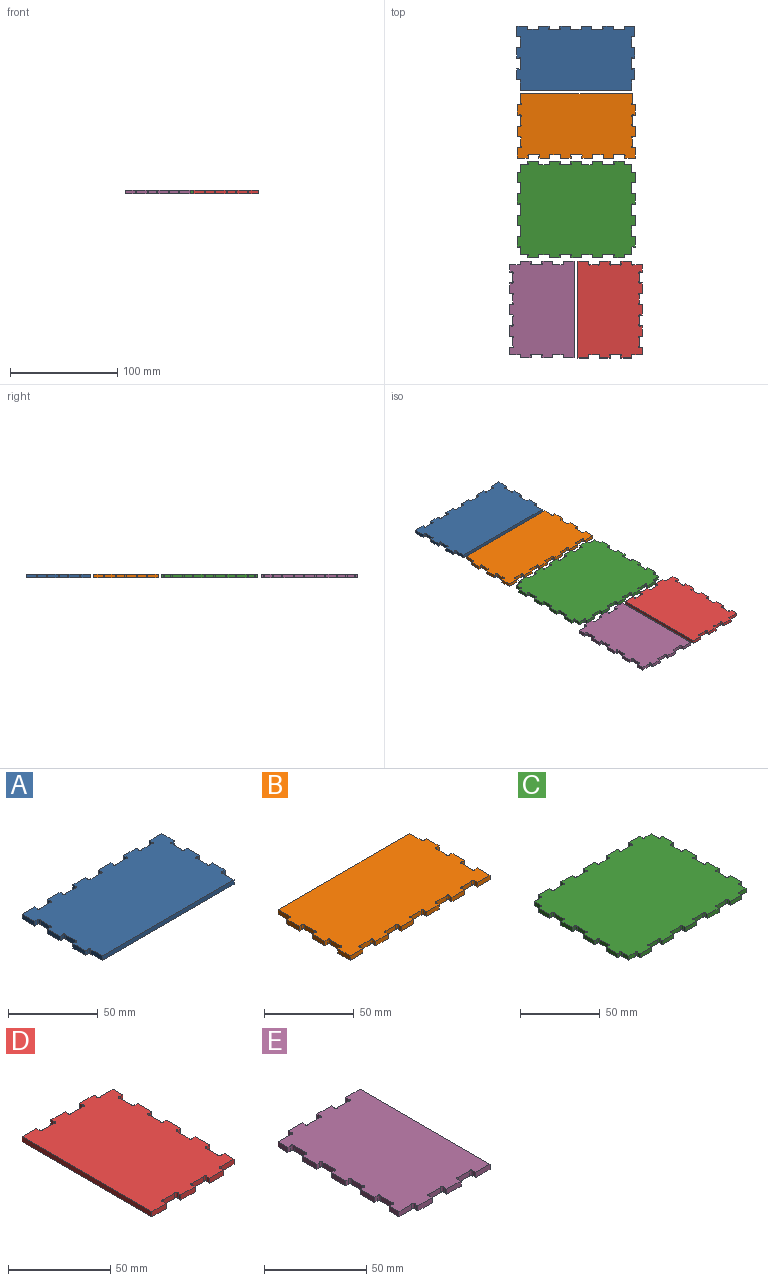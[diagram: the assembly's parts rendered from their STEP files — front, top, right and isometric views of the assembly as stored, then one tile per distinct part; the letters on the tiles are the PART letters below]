
ASSEMBLY  parts=5 mates=4
PART A: 66 faces, bbox 110x60x3.1 mm
  f0: plane 110x60mm, normal (0,0,-1), area 6247.3mm2, adj f1,f2,f3,f4,f5,f6,f7,f8
  f1: plane 7.64x3.1mm, normal (0,1,0), area 23.7mm2, adj f0,f17,f34,f65
  f2: plane 3.1x1.87mm, normal (1,0,0), area 5.8mm2, adj f0,f17,f21,f34
  f3: plane 7.64x3.1mm, normal (0,1,0), area 23.7mm2, adj f0,f17,f32,f33
  f4: plane 3.1x1.87mm, normal (-1,0,0), area 5.8mm2, adj f0,f17,f21,f33
  f5: plane 3.1x1.87mm, normal (1,0,0), area 5.8mm2, adj f0,f17,f20,f32
  f6: plane 7.64x3.1mm, normal (0,1,0), area 23.7mm2, adj f0,f17,f30,f31
  f7: plane 3.1x1.87mm, normal (-1,0,0), area 5.8mm2, adj f0,f17,f20,f31
  f8: plane 3.1x1.87mm, normal (1,0,0), area 5.8mm2, adj f0,f17,f19,f30
  f9: plane 7.64x3.1mm, normal (-1,0,0), area 23.7mm2, adj f0,f17,f28,f29
  f10: plane 3.1x1.87mm, normal (0,-1,0), area 5.8mm2, adj f0,f17,f22,f29
  f11: plane 3.1x1.87mm, normal (0,1,0), area 5.8mm2, adj f0,f17,f23,f28
  f12: plane 7.64x3.1mm, normal (-1,0,0), area 23.7mm2, adj f0,f17,f26,f27
  f13: plane 3.1x1.87mm, normal (0,-1,0), area 5.8mm2, adj f0,f17,f23,f27
  f14: plane 3.1x1.87mm, normal (0,1,0), area 5.8mm2, adj f0,f17,f24,f26
  f15: plane 8.82x3.1mm, normal (-1,0,0), area 27.3mm2, adj f0,f17,f18,f25
  f16: plane 3.1x1.87mm, normal (0,-1,0), area 5.8mm2, adj f0,f17,f24,f25
  f17: plane 110x60mm, normal (0,0,1), area 6247.3mm2, adj f1,f2,f3,f4,f5,f6,f7,f8
  f18: plane 103.8x3.1mm, normal (0,-1,0), area 321.8mm2, adj f0,f15,f17,f48
  f19: plane 9.95x3.1mm, normal (0,1,0), area 30.8mm2, adj f0,f8,f17,f22
  f20: plane 9.9x3.1mm, normal (0,1,0), area 30.7mm2, adj f0,f5,f7,f17
  f21: plane 9.9x3.1mm, normal (0,1,0), area 30.7mm2, adj f0,f2,f4,f17
  f22: plane 9.95x3.1mm, normal (-1,0,0), area 30.8mm2, adj f0,f10,f17,f19
  f23: plane 9.9x3.1mm, normal (-1,0,0), area 30.7mm2, adj f0,f11,f13,f17
  f24: plane 9.9x3.1mm, normal (-1,0,0), area 30.7mm2, adj f0,f14,f16,f17
  f25: cylinder r=0.87mm len=3.1mm, axis (0,0,1), area 8.5mm2, adj f0,f15,f16,f17
  f26: cylinder r=0.87mm len=3.1mm, axis (0,0,1), area 8.5mm2, adj f0,f12,f14,f17
  f27: cylinder r=0.87mm len=3.1mm, axis (0,0,1), area 8.5mm2, adj f0,f12,f13,f17
  f28: cylinder r=0.87mm len=3.1mm, axis (0,0,1), area 8.5mm2, adj f0,f9,f11,f17
  f29: cylinder r=0.87mm len=3.1mm, axis (0,0,1), area 8.5mm2, adj f0,f9,f10,f17
  f30: cylinder r=0.87mm len=3.1mm, axis (0,0,1), area 8.5mm2, adj f0,f6,f8,f17
  f31: cylinder r=0.87mm len=3.1mm, axis (0,0,1), area 8.5mm2, adj f0,f6,f7,f17
  f32: cylinder r=0.87mm len=3.1mm, axis (0,0,1), area 8.5mm2, adj f0,f3,f5,f17
  f33: cylinder r=0.87mm len=3.1mm, axis (0,0,1), area 8.5mm2, adj f0,f3,f4,f17
  f34: cylinder r=0.87mm len=3.1mm, axis (0,0,1), area 8.5mm2, adj f0,f1,f2,f17
  f35: plane 3.1x1.87mm, normal (-1,0,0), area 5.8mm2, adj f0,f17,f52,f65
  f36: plane 7.64x3.1mm, normal (0,1,0), area 23.7mm2, adj f0,f17,f63,f64
  f37: plane 3.1x1.87mm, normal (1,0,0), area 5.8mm2, adj f0,f17,f52,f64
  f38: plane 3.1x1.87mm, normal (-1,0,0), area 5.8mm2, adj f0,f17,f51,f63
  f39: plane 7.64x3.1mm, normal (0,1,0), area 23.7mm2, adj f0,f17,f61,f62
  f40: plane 3.1x1.87mm, normal (1,0,0), area 5.8mm2, adj f0,f17,f51,f62
  f41: plane 3.1x1.87mm, normal (-1,0,0), area 5.8mm2, adj f0,f17,f50,f61
  f42: plane 7.64x3.1mm, normal (1,0,0), area 23.7mm2, adj f0,f17,f59,f60
  f43: plane 3.1x1.87mm, normal (0,-1,0), area 5.8mm2, adj f0,f17,f53,f60
  f44: plane 3.1x1.87mm, normal (0,1,0), area 5.8mm2, adj f0,f17,f54,f59
  f45: plane 7.64x3.1mm, normal (1,0,0), area 23.7mm2, adj f0,f17,f57,f58
  f46: plane 3.1x1.87mm, normal (0,-1,0), area 5.8mm2, adj f0,f17,f54,f58
  f47: plane 3.1x1.87mm, normal (0,1,0), area 5.8mm2, adj f0,f17,f55,f57
  f48: plane 8.82x3.1mm, normal (1,0,0), area 27.3mm2, adj f0,f17,f18,f56
  f49: plane 3.1x1.87mm, normal (0,-1,0), area 5.8mm2, adj f0,f17,f55,f56
  f50: plane 9.95x3.1mm, normal (0,1,0), area 30.8mm2, adj f0,f17,f41,f53
  f51: plane 9.9x3.1mm, normal (0,1,0), area 30.7mm2, adj f0,f17,f38,f40
  f52: plane 9.9x3.1mm, normal (0,1,0), area 30.7mm2, adj f0,f17,f35,f37
  f53: plane 9.95x3.1mm, normal (1,0,0), area 30.8mm2, adj f0,f17,f43,f50
  f54: plane 9.9x3.1mm, normal (1,0,0), area 30.7mm2, adj f0,f17,f44,f46
  f55: plane 9.9x3.1mm, normal (1,0,0), area 30.7mm2, adj f0,f17,f47,f49
  f56: cylinder r=0.87mm len=3.1mm, axis (0,0,1), area 8.5mm2, adj f0,f17,f48,f49
  f57: cylinder r=0.87mm len=3.1mm, axis (0,0,1), area 8.5mm2, adj f0,f17,f45,f47
  f58: cylinder r=0.87mm len=3.1mm, axis (0,0,1), area 8.5mm2, adj f0,f17,f45,f46
  f59: cylinder r=0.87mm len=3.1mm, axis (0,0,1), area 8.5mm2, adj f0,f17,f42,f44
  f60: cylinder r=0.87mm len=3.1mm, axis (0,0,1), area 8.5mm2, adj f0,f17,f42,f43
  f61: cylinder r=0.87mm len=3.1mm, axis (0,0,1), area 8.5mm2, adj f0,f17,f39,f41
  f62: cylinder r=0.87mm len=3.1mm, axis (0,0,1), area 8.5mm2, adj f0,f17,f39,f40
  f63: cylinder r=0.87mm len=3.1mm, axis (0,0,1), area 8.5mm2, adj f0,f17,f36,f38
  f64: cylinder r=0.87mm len=3.1mm, axis (0,0,1), area 8.5mm2, adj f0,f17,f36,f37
  f65: cylinder r=0.87mm len=3.1mm, axis (0,0,1), area 8.5mm2, adj f0,f1,f17,f35
PART B: 66 faces, bbox 110x60x3.1 mm
  f0: plane 110x60mm, normal (0,0,-1), area 6247.3mm2, adj f1,f2,f3,f4,f5,f6,f7,f8
  f1: plane 7.64x3.1mm, normal (0,-1,0), area 23.7mm2, adj f0,f17,f34,f65
  f2: plane 3.1x1.87mm, normal (1,0,0), area 5.8mm2, adj f0,f17,f21,f34
  f3: plane 7.64x3.1mm, normal (0,-1,0), area 23.7mm2, adj f0,f17,f32,f33
  f4: plane 3.1x1.87mm, normal (-1,0,0), area 5.8mm2, adj f0,f17,f21,f33
  f5: plane 3.1x1.87mm, normal (1,0,0), area 5.8mm2, adj f0,f17,f20,f32
  f6: plane 7.64x3.1mm, normal (0,-1,0), area 23.7mm2, adj f0,f17,f30,f31
  f7: plane 3.1x1.87mm, normal (-1,0,0), area 5.8mm2, adj f0,f17,f20,f31
  f8: plane 3.1x1.87mm, normal (1,0,0), area 5.8mm2, adj f0,f17,f19,f30
  f9: plane 7.64x3.1mm, normal (-1,0,0), area 23.7mm2, adj f0,f17,f28,f29
  f10: plane 3.1x1.87mm, normal (0,1,0), area 5.8mm2, adj f0,f17,f22,f29
  f11: plane 3.1x1.87mm, normal (0,-1,0), area 5.8mm2, adj f0,f17,f23,f28
  f12: plane 7.64x3.1mm, normal (-1,0,0), area 23.7mm2, adj f0,f17,f26,f27
  f13: plane 3.1x1.87mm, normal (0,1,0), area 5.8mm2, adj f0,f17,f23,f27
  f14: plane 3.1x1.87mm, normal (0,-1,0), area 5.8mm2, adj f0,f17,f24,f26
  f15: plane 8.82x3.1mm, normal (-1,0,0), area 27.3mm2, adj f0,f17,f18,f25
  f16: plane 3.1x1.87mm, normal (0,1,0), area 5.8mm2, adj f0,f17,f24,f25
  f17: plane 110x60mm, normal (0,0,1), area 6247.3mm2, adj f1,f2,f3,f4,f5,f6,f7,f8
  f18: plane 103.8x3.1mm, normal (0,1,0), area 321.8mm2, adj f0,f15,f17,f48
  f19: plane 9.95x3.1mm, normal (0,-1,0), area 30.8mm2, adj f0,f8,f17,f22
  f20: plane 9.9x3.1mm, normal (0,-1,0), area 30.7mm2, adj f0,f5,f7,f17
  f21: plane 9.9x3.1mm, normal (0,-1,0), area 30.7mm2, adj f0,f2,f4,f17
  f22: plane 9.95x3.1mm, normal (-1,0,0), area 30.8mm2, adj f0,f10,f17,f19
  f23: plane 9.9x3.1mm, normal (-1,0,0), area 30.7mm2, adj f0,f11,f13,f17
  f24: plane 9.9x3.1mm, normal (-1,0,0), area 30.7mm2, adj f0,f14,f16,f17
  f25: cylinder r=0.87mm len=3.1mm, axis (0,0,1), area 8.5mm2, adj f0,f15,f16,f17
  f26: cylinder r=0.87mm len=3.1mm, axis (0,0,1), area 8.5mm2, adj f0,f12,f14,f17
  f27: cylinder r=0.87mm len=3.1mm, axis (0,0,1), area 8.5mm2, adj f0,f12,f13,f17
  f28: cylinder r=0.87mm len=3.1mm, axis (0,0,1), area 8.5mm2, adj f0,f9,f11,f17
  f29: cylinder r=0.87mm len=3.1mm, axis (0,0,1), area 8.5mm2, adj f0,f9,f10,f17
  f30: cylinder r=0.87mm len=3.1mm, axis (0,0,1), area 8.5mm2, adj f0,f6,f8,f17
  f31: cylinder r=0.87mm len=3.1mm, axis (0,0,1), area 8.5mm2, adj f0,f6,f7,f17
  f32: cylinder r=0.87mm len=3.1mm, axis (0,0,1), area 8.5mm2, adj f0,f3,f5,f17
  f33: cylinder r=0.87mm len=3.1mm, axis (0,0,1), area 8.5mm2, adj f0,f3,f4,f17
  f34: cylinder r=0.87mm len=3.1mm, axis (0,0,1), area 8.5mm2, adj f0,f1,f2,f17
  f35: plane 3.1x1.87mm, normal (-1,0,0), area 5.8mm2, adj f0,f17,f52,f65
  f36: plane 7.64x3.1mm, normal (0,-1,0), area 23.7mm2, adj f0,f17,f63,f64
  f37: plane 3.1x1.87mm, normal (1,0,0), area 5.8mm2, adj f0,f17,f52,f64
  f38: plane 3.1x1.87mm, normal (-1,0,0), area 5.8mm2, adj f0,f17,f51,f63
  f39: plane 7.64x3.1mm, normal (0,-1,0), area 23.7mm2, adj f0,f17,f61,f62
  f40: plane 3.1x1.87mm, normal (1,0,0), area 5.8mm2, adj f0,f17,f51,f62
  f41: plane 3.1x1.87mm, normal (-1,0,0), area 5.8mm2, adj f0,f17,f50,f61
  f42: plane 7.64x3.1mm, normal (1,0,0), area 23.7mm2, adj f0,f17,f59,f60
  f43: plane 3.1x1.87mm, normal (0,1,0), area 5.8mm2, adj f0,f17,f53,f60
  f44: plane 3.1x1.87mm, normal (0,-1,0), area 5.8mm2, adj f0,f17,f54,f59
  f45: plane 7.64x3.1mm, normal (1,0,0), area 23.7mm2, adj f0,f17,f57,f58
  f46: plane 3.1x1.87mm, normal (0,1,0), area 5.8mm2, adj f0,f17,f54,f58
  f47: plane 3.1x1.87mm, normal (0,-1,0), area 5.8mm2, adj f0,f17,f55,f57
  f48: plane 8.82x3.1mm, normal (1,0,0), area 27.3mm2, adj f0,f17,f18,f56
  f49: plane 3.1x1.87mm, normal (0,1,0), area 5.8mm2, adj f0,f17,f55,f56
  f50: plane 9.95x3.1mm, normal (0,-1,0), area 30.8mm2, adj f0,f17,f41,f53
  f51: plane 9.9x3.1mm, normal (0,-1,0), area 30.7mm2, adj f0,f17,f38,f40
  f52: plane 9.9x3.1mm, normal (0,-1,0), area 30.7mm2, adj f0,f17,f35,f37
  f53: plane 9.95x3.1mm, normal (1,0,0), area 30.8mm2, adj f0,f17,f43,f50
  f54: plane 9.9x3.1mm, normal (1,0,0), area 30.7mm2, adj f0,f17,f44,f46
  f55: plane 9.9x3.1mm, normal (1,0,0), area 30.7mm2, adj f0,f17,f47,f49
  f56: cylinder r=0.87mm len=3.1mm, axis (0,0,1), area 8.5mm2, adj f0,f17,f48,f49
  f57: cylinder r=0.87mm len=3.1mm, axis (0,0,1), area 8.5mm2, adj f0,f17,f45,f47
  f58: cylinder r=0.87mm len=3.1mm, axis (0,0,1), area 8.5mm2, adj f0,f17,f45,f46
  f59: cylinder r=0.87mm len=3.1mm, axis (0,0,1), area 8.5mm2, adj f0,f17,f42,f44
  f60: cylinder r=0.87mm len=3.1mm, axis (0,0,1), area 8.5mm2, adj f0,f17,f42,f43
  f61: cylinder r=0.87mm len=3.1mm, axis (0,0,1), area 8.5mm2, adj f0,f17,f39,f41
  f62: cylinder r=0.87mm len=3.1mm, axis (0,0,1), area 8.5mm2, adj f0,f17,f39,f40
  f63: cylinder r=0.87mm len=3.1mm, axis (0,0,1), area 8.5mm2, adj f0,f17,f36,f38
  f64: cylinder r=0.87mm len=3.1mm, axis (0,0,1), area 8.5mm2, adj f0,f17,f36,f37
  f65: cylinder r=0.87mm len=3.1mm, axis (0,0,1), area 8.5mm2, adj f0,f1,f17,f35
PART C: 114 faces, bbox 110x90x3.1 mm
  f0: plane 7.64x3.1mm, normal (-1,0,0), area 23.7mm2, adj f15,f16,f30,f113
  f1: plane 3.1x1.87mm, normal (0,-1,0), area 5.8mm2, adj f15,f16,f21,f30
  f2: plane 7.64x3.1mm, normal (-1,0,0), area 23.7mm2, adj f15,f16,f28,f29
  f3: plane 3.1x1.87mm, normal (0,1,0), area 5.8mm2, adj f15,f16,f21,f29
  f4: plane 3.1x1.87mm, normal (0,-1,0), area 5.8mm2, adj f15,f16,f20,f28
  f5: plane 5.72x3.1mm, normal (-1,0,0), area 17.7mm2, adj f7,f15,f16,f27
  f6: plane 3.1x1.87mm, normal (0,1,0), area 5.8mm2, adj f15,f16,f20,f27
  f7: plane 5.72x3.1mm, normal (0,1,0), area 17.7mm2, adj f5,f15,f16,f26
  f8: plane 3.1x1.87mm, normal (-1,0,0), area 5.8mm2, adj f15,f16,f17,f26
  f9: plane 7.64x3.1mm, normal (0,1,0), area 23.7mm2, adj f15,f16,f24,f25
  f10: plane 3.1x1.87mm, normal (1,0,0), area 5.8mm2, adj f15,f16,f17,f25
  f11: plane 3.1x1.87mm, normal (-1,0,0), area 5.8mm2, adj f15,f16,f18,f24
  f12: plane 7.64x3.1mm, normal (0,1,0), area 23.7mm2, adj f15,f16,f22,f23
  f13: plane 3.1x1.87mm, normal (-1,0,0), area 5.8mm2, adj f15,f16,f19,f23
  f14: plane 3.1x1.87mm, normal (1,0,0), area 5.8mm2, adj f15,f16,f18,f22
  f15: plane 110x90mm, normal (0,0,1), area 9235.3mm2, adj f0,f1,f2,f3,f4,f5,f6,f7
  f16: plane 110x90mm, normal (0,0,-1), area 9235.3mm2, adj f0,f1,f2,f3,f4,f5,f6,f7
  f17: plane 9.9x3.1mm, normal (0,1,0), area 30.7mm2, adj f8,f10,f15,f16
  f18: plane 9.9x3.1mm, normal (0,1,0), area 30.7mm2, adj f11,f14,f15,f16
  f19: plane 9.9x3.1mm, normal (0,1,0), area 30.7mm2, adj f13,f15,f16,f44
  f20: plane 9.9x3.1mm, normal (-1,0,0), area 30.7mm2, adj f4,f6,f15,f16
  f21: plane 9.9x3.1mm, normal (-1,0,0), area 30.7mm2, adj f1,f3,f15,f16
  f22: cylinder r=0.87mm len=3.1mm, axis (0,0,1), area 8.5mm2, adj f12,f14,f15,f16
  f23: cylinder r=0.87mm len=3.1mm, axis (0,0,1), area 8.5mm2, adj f12,f13,f15,f16
  f24: cylinder r=0.87mm len=3.1mm, axis (0,0,1), area 8.5mm2, adj f9,f11,f15,f16
  f25: cylinder r=0.87mm len=3.1mm, axis (0,0,1), area 8.5mm2, adj f9,f10,f15,f16
  f26: cylinder r=0.87mm len=3.1mm, axis (0,0,1), area 8.5mm2, adj f7,f8,f15,f16
  f27: cylinder r=0.87mm len=3.1mm, axis (0,0,1), area 8.5mm2, adj f5,f6,f15,f16
  f28: cylinder r=0.87mm len=3.1mm, axis (0,0,1), area 8.5mm2, adj f2,f4,f15,f16
  f29: cylinder r=0.87mm len=3.1mm, axis (0,0,1), area 8.5mm2, adj f2,f3,f15,f16
  f30: cylinder r=0.87mm len=3.1mm, axis (0,0,1), area 8.5mm2, adj f0,f1,f15,f16
  f31: plane 7.64x3.1mm, normal (1,0,0), area 23.7mm2, adj f15,f16,f58,f86
  f32: plane 3.1x1.87mm, normal (0,-1,0), area 5.8mm2, adj f15,f16,f49,f58
  f33: plane 7.64x3.1mm, normal (1,0,0), area 23.7mm2, adj f15,f16,f56,f57
  f34: plane 3.1x1.87mm, normal (0,1,0), area 5.8mm2, adj f15,f16,f49,f57
  f35: plane 3.1x1.87mm, normal (0,-1,0), area 5.8mm2, adj f15,f16,f48,f56
  f36: plane 5.72x3.1mm, normal (1,0,0), area 17.7mm2, adj f15,f16,f38,f55
  f37: plane 3.1x1.87mm, normal (0,1,0), area 5.8mm2, adj f15,f16,f48,f55
  f38: plane 5.72x3.1mm, normal (0,1,0), area 17.7mm2, adj f15,f16,f36,f54
  f39: plane 3.1x1.87mm, normal (1,0,0), area 5.8mm2, adj f15,f16,f46,f54
  f40: plane 7.64x3.1mm, normal (0,1,0), area 23.7mm2, adj f15,f16,f52,f53
  f41: plane 3.1x1.87mm, normal (-1,0,0), area 5.8mm2, adj f15,f16,f46,f53
  f42: plane 3.1x1.87mm, normal (1,0,0), area 5.8mm2, adj f15,f16,f47,f52
  f43: plane 7.64x3.1mm, normal (0,1,0), area 23.7mm2, adj f15,f16,f50,f51
  f44: plane 3.1x1.87mm, normal (1,0,0), area 5.8mm2, adj f15,f16,f19,f51
  f45: plane 3.1x1.87mm, normal (-1,0,0), area 5.8mm2, adj f15,f16,f47,f50
  f46: plane 9.9x3.1mm, normal (0,1,0), area 30.7mm2, adj f15,f16,f39,f41
  f47: plane 9.9x3.1mm, normal (0,1,0), area 30.7mm2, adj f15,f16,f42,f45
  f48: plane 9.9x3.1mm, normal (1,0,0), area 30.7mm2, adj f15,f16,f35,f37
  f49: plane 9.9x3.1mm, normal (1,0,0), area 30.7mm2, adj f15,f16,f32,f34
  f50: cylinder r=0.87mm len=3.1mm, axis (0,0,1), area 8.5mm2, adj f15,f16,f43,f45
  f51: cylinder r=0.87mm len=3.1mm, axis (0,0,1), area 8.5mm2, adj f15,f16,f43,f44
  f52: cylinder r=0.87mm len=3.1mm, axis (0,0,1), area 8.5mm2, adj f15,f16,f40,f42
  f53: cylinder r=0.87mm len=3.1mm, axis (0,0,1), area 8.5mm2, adj f15,f16,f40,f41
  f54: cylinder r=0.87mm len=3.1mm, axis (0,0,1), area 8.5mm2, adj f15,f16,f38,f39
  f55: cylinder r=0.87mm len=3.1mm, axis (0,0,1), area 8.5mm2, adj f15,f16,f36,f37
  f56: cylinder r=0.87mm len=3.1mm, axis (0,0,1), area 8.5mm2, adj f15,f16,f33,f35
  f57: cylinder r=0.87mm len=3.1mm, axis (0,0,1), area 8.5mm2, adj f15,f16,f33,f34
  f58: cylinder r=0.87mm len=3.1mm, axis (0,0,1), area 8.5mm2, adj f15,f16,f31,f32
  f59: plane 3.1x1.87mm, normal (0,1,0), area 5.8mm2, adj f15,f16,f77,f86
  f60: plane 7.64x3.1mm, normal (1,0,0), area 23.7mm2, adj f15,f16,f84,f85
  f61: plane 3.1x1.87mm, normal (0,-1,0), area 5.8mm2, adj f15,f16,f77,f85
  f62: plane 3.1x1.87mm, normal (0,1,0), area 5.8mm2, adj f15,f16,f76,f84
  f63: plane 5.72x3.1mm, normal (1,0,0), area 17.7mm2, adj f15,f16,f65,f83
  f64: plane 3.1x1.87mm, normal (0,-1,0), area 5.8mm2, adj f15,f16,f76,f83
  f65: plane 5.72x3.1mm, normal (0,-1,0), area 17.7mm2, adj f15,f16,f63,f82
  f66: plane 3.1x1.87mm, normal (1,0,0), area 5.8mm2, adj f15,f16,f73,f82
  f67: plane 7.64x3.1mm, normal (0,-1,0), area 23.7mm2, adj f15,f16,f80,f81
  f68: plane 3.1x1.87mm, normal (-1,0,0), area 5.8mm2, adj f15,f16,f73,f81
  f69: plane 3.1x1.87mm, normal (1,0,0), area 5.8mm2, adj f15,f16,f74,f80
  f70: plane 7.64x3.1mm, normal (0,-1,0), area 23.7mm2, adj f15,f16,f78,f79
  f71: plane 3.1x1.87mm, normal (1,0,0), area 5.8mm2, adj f15,f16,f75,f79
  f72: plane 3.1x1.87mm, normal (-1,0,0), area 5.8mm2, adj f15,f16,f74,f78
  f73: plane 9.9x3.1mm, normal (0,-1,0), area 30.7mm2, adj f15,f16,f66,f68
  f74: plane 9.9x3.1mm, normal (0,-1,0), area 30.7mm2, adj f15,f16,f69,f72
  f75: plane 9.9x3.1mm, normal (0,-1,0), area 30.7mm2, adj f15,f16,f71,f99
  f76: plane 9.9x3.1mm, normal (1,0,0), area 30.7mm2, adj f15,f16,f62,f64
  f77: plane 9.9x3.1mm, normal (1,0,0), area 30.7mm2, adj f15,f16,f59,f61
  f78: cylinder r=0.87mm len=3.1mm, axis (0,0,1), area 8.5mm2, adj f15,f16,f70,f72
  f79: cylinder r=0.87mm len=3.1mm, axis (0,0,1), area 8.5mm2, adj f15,f16,f70,f71
  f80: cylinder r=0.87mm len=3.1mm, axis (0,0,1), area 8.5mm2, adj f15,f16,f67,f69
  f81: cylinder r=0.87mm len=3.1mm, axis (0,0,1), area 8.5mm2, adj f15,f16,f67,f68
  f82: cylinder r=0.87mm len=3.1mm, axis (0,0,1), area 8.5mm2, adj f15,f16,f65,f66
  f83: cylinder r=0.87mm len=3.1mm, axis (0,0,1), area 8.5mm2, adj f15,f16,f63,f64
  f84: cylinder r=0.87mm len=3.1mm, axis (0,0,1), area 8.5mm2, adj f15,f16,f60,f62
  f85: cylinder r=0.87mm len=3.1mm, axis (0,0,1), area 8.5mm2, adj f15,f16,f60,f61
  f86: cylinder r=0.87mm len=3.1mm, axis (0,0,1), area 8.5mm2, adj f15,f16,f31,f59
  f87: plane 3.1x1.87mm, normal (0,1,0), area 5.8mm2, adj f15,f16,f104,f113
  f88: plane 7.64x3.1mm, normal (-1,0,0), area 23.7mm2, adj f15,f16,f111,f112
  f89: plane 3.1x1.87mm, normal (0,-1,0), area 5.8mm2, adj f15,f16,f104,f112
  f90: plane 3.1x1.87mm, normal (0,1,0), area 5.8mm2, adj f15,f16,f103,f111
  f91: plane 5.72x3.1mm, normal (-1,0,0), area 17.7mm2, adj f15,f16,f93,f110
  f92: plane 3.1x1.87mm, normal (0,-1,0), area 5.8mm2, adj f15,f16,f103,f110
  f93: plane 5.72x3.1mm, normal (0,-1,0), area 17.7mm2, adj f15,f16,f91,f109
  f94: plane 3.1x1.87mm, normal (-1,0,0), area 5.8mm2, adj f15,f16,f101,f109
  f95: plane 7.64x3.1mm, normal (0,-1,0), area 23.7mm2, adj f15,f16,f107,f108
  f96: plane 3.1x1.87mm, normal (1,0,0), area 5.8mm2, adj f15,f16,f101,f108
  f97: plane 3.1x1.87mm, normal (-1,0,0), area 5.8mm2, adj f15,f16,f102,f107
  f98: plane 7.64x3.1mm, normal (0,-1,0), area 23.7mm2, adj f15,f16,f105,f106
  f99: plane 3.1x1.87mm, normal (-1,0,0), area 5.8mm2, adj f15,f16,f75,f106
  f100: plane 3.1x1.87mm, normal (1,0,0), area 5.8mm2, adj f15,f16,f102,f105
  f101: plane 9.9x3.1mm, normal (0,-1,0), area 30.7mm2, adj f15,f16,f94,f96
  f102: plane 9.9x3.1mm, normal (0,-1,0), area 30.7mm2, adj f15,f16,f97,f100
  f103: plane 9.9x3.1mm, normal (-1,0,0), area 30.7mm2, adj f15,f16,f90,f92
  f104: plane 9.9x3.1mm, normal (-1,0,0), area 30.7mm2, adj f15,f16,f87,f89
  f105: cylinder r=0.87mm len=3.1mm, axis (0,0,1), area 8.5mm2, adj f15,f16,f98,f100
  f106: cylinder r=0.87mm len=3.1mm, axis (0,0,1), area 8.5mm2, adj f15,f16,f98,f99
  f107: cylinder r=0.87mm len=3.1mm, axis (0,0,1), area 8.5mm2, adj f15,f16,f95,f97
  f108: cylinder r=0.87mm len=3.1mm, axis (0,0,1), area 8.5mm2, adj f15,f16,f95,f96
  f109: cylinder r=0.87mm len=3.1mm, axis (0,0,1), area 8.5mm2, adj f15,f16,f93,f94
  f110: cylinder r=0.87mm len=3.1mm, axis (0,0,1), area 8.5mm2, adj f15,f16,f91,f92
  f111: cylinder r=0.87mm len=3.1mm, axis (0,0,1), area 8.5mm2, adj f15,f16,f88,f90
  f112: cylinder r=0.87mm len=3.1mm, axis (0,0,1), area 8.5mm2, adj f15,f16,f88,f89
  f113: cylinder r=0.87mm len=3.1mm, axis (0,0,1), area 8.5mm2, adj f0,f15,f16,f87
PART D: 60 faces, bbox 60x90x3.1 mm
  f0: plane 7.64x3.1mm, normal (1,0,0), area 23.7mm2, adj f15,f16,f30,f31
  f1: plane 3.1x1.87mm, normal (0,-1,0), area 5.8mm2, adj f15,f16,f19,f31
  f2: plane 3.1x1.87mm, normal (0,1,0), area 5.8mm2, adj f15,f16,f18,f30
  f3: plane 7.64x3.1mm, normal (1,0,0), area 23.7mm2, adj f15,f16,f28,f29
  f4: plane 3.1x1.87mm, normal (0,-1,0), area 5.8mm2, adj f15,f16,f18,f29
  f5: plane 3.1x1.87mm, normal (0,1,0), area 5.8mm2, adj f14,f15,f16,f28
  f6: plane 8.82x3.1mm, normal (0,-1,0), area 27.3mm2, adj f14,f15,f16,f27
  f7: plane 3.1x1.87mm, normal (1,0,0), area 5.8mm2, adj f15,f16,f20,f27
  f8: plane 7.64x3.1mm, normal (0,-1,0), area 23.7mm2, adj f15,f16,f25,f26
  f9: plane 3.1x1.87mm, normal (-1,0,0), area 5.8mm2, adj f15,f16,f20,f26
  f10: plane 3.1x1.87mm, normal (1,0,0), area 5.8mm2, adj f15,f16,f21,f25
  f11: plane 7.64x3.1mm, normal (0,-1,0), area 23.7mm2, adj f15,f16,f23,f24
  f12: plane 3.1x1.87mm, normal (-1,0,0), area 5.8mm2, adj f15,f16,f21,f24
  f13: plane 3.1x1.87mm, normal (1,0,0), area 5.8mm2, adj f15,f16,f22,f23
  f14: plane 6.85x3.1mm, normal (1,0,0), area 21.2mm2, adj f5,f6,f15,f16
  f15: plane 90x60mm, normal (0,0,-1), area 5079.4mm2, adj f0,f1,f2,f3,f4,f5,f6,f7
  f16: plane 90x60mm, normal (0,0,1), area 5079.4mm2, adj f0,f1,f2,f3,f4,f5,f6,f7
  f17: plane 90x3.1mm, normal (-1,0,0), area 279mm2, adj f15,f16,f22,f50
  f18: plane 9.9x3.1mm, normal (1,0,0), area 30.7mm2, adj f2,f4,f15,f16
  f19: plane 9.9x3.1mm, normal (1,0,0), area 30.7mm2, adj f1,f15,f16,f33
  f20: plane 9.9x3.1mm, normal (0,-1,0), area 30.7mm2, adj f7,f9,f15,f16
  f21: plane 9.9x3.1mm, normal (0,-1,0), area 30.7mm2, adj f10,f12,f15,f16
  f22: plane 9.95x3.1mm, normal (0,-1,0), area 30.8mm2, adj f13,f15,f16,f17
  f23: cylinder r=0.87mm len=3.1mm, axis (0,0,1), area 8.5mm2, adj f11,f13,f15,f16
  f24: cylinder r=0.87mm len=3.1mm, axis (0,0,1), area 8.5mm2, adj f11,f12,f15,f16
  f25: cylinder r=0.87mm len=3.1mm, axis (0,0,1), area 8.5mm2, adj f8,f10,f15,f16
  f26: cylinder r=0.87mm len=3.1mm, axis (0,0,1), area 8.5mm2, adj f8,f9,f15,f16
  f27: cylinder r=0.87mm len=3.1mm, axis (0,0,1), area 8.5mm2, adj f6,f7,f15,f16
  f28: cylinder r=0.87mm len=3.1mm, axis (0,0,1), area 8.5mm2, adj f3,f5,f15,f16
  f29: cylinder r=0.87mm len=3.1mm, axis (0,0,1), area 8.5mm2, adj f3,f4,f15,f16
  f30: cylinder r=0.87mm len=3.1mm, axis (0,0,1), area 8.5mm2, adj f0,f2,f15,f16
  f31: cylinder r=0.87mm len=3.1mm, axis (0,0,1), area 8.5mm2, adj f0,f1,f15,f16
  f32: plane 7.64x3.1mm, normal (1,0,0), area 23.7mm2, adj f15,f16,f58,f59
  f33: plane 3.1x1.87mm, normal (0,1,0), area 5.8mm2, adj f15,f16,f19,f59
  f34: plane 3.1x1.87mm, normal (0,-1,0), area 5.8mm2, adj f15,f16,f47,f58
  f35: plane 7.64x3.1mm, normal (1,0,0), area 23.7mm2, adj f15,f16,f56,f57
  f36: plane 3.1x1.87mm, normal (0,1,0), area 5.8mm2, adj f15,f16,f47,f57
  f37: plane 3.1x1.87mm, normal (0,-1,0), area 5.8mm2, adj f15,f16,f46,f56
  f38: plane 8.82x3.1mm, normal (0,1,0), area 27.3mm2, adj f15,f16,f46,f55
  f39: plane 3.1x1.87mm, normal (1,0,0), area 5.8mm2, adj f15,f16,f48,f55
  f40: plane 7.64x3.1mm, normal (0,1,0), area 23.7mm2, adj f15,f16,f53,f54
  f41: plane 3.1x1.87mm, normal (-1,0,0), area 5.8mm2, adj f15,f16,f48,f54
  f42: plane 3.1x1.87mm, normal (1,0,0), area 5.8mm2, adj f15,f16,f49,f53
  f43: plane 7.64x3.1mm, normal (0,1,0), area 23.7mm2, adj f15,f16,f51,f52
  f44: plane 3.1x1.87mm, normal (-1,0,0), area 5.8mm2, adj f15,f16,f49,f52
  f45: plane 3.1x1.87mm, normal (1,0,0), area 5.8mm2, adj f15,f16,f50,f51
  f46: plane 6.85x3.1mm, normal (1,0,0), area 21.2mm2, adj f15,f16,f37,f38
  f47: plane 9.9x3.1mm, normal (1,0,0), area 30.7mm2, adj f15,f16,f34,f36
  f48: plane 9.9x3.1mm, normal (0,1,0), area 30.7mm2, adj f15,f16,f39,f41
  f49: plane 9.9x3.1mm, normal (0,1,0), area 30.7mm2, adj f15,f16,f42,f44
  f50: plane 9.95x3.1mm, normal (0,1,0), area 30.8mm2, adj f15,f16,f17,f45
  f51: cylinder r=0.87mm len=3.1mm, axis (0,0,1), area 8.5mm2, adj f15,f16,f43,f45
  f52: cylinder r=0.87mm len=3.1mm, axis (0,0,1), area 8.5mm2, adj f15,f16,f43,f44
  f53: cylinder r=0.87mm len=3.1mm, axis (0,0,1), area 8.5mm2, adj f15,f16,f40,f42
  f54: cylinder r=0.87mm len=3.1mm, axis (0,0,1), area 8.5mm2, adj f15,f16,f40,f41
  f55: cylinder r=0.87mm len=3.1mm, axis (0,0,1), area 8.5mm2, adj f15,f16,f38,f39
  f56: cylinder r=0.87mm len=3.1mm, axis (0,0,1), area 8.5mm2, adj f15,f16,f35,f37
  f57: cylinder r=0.87mm len=3.1mm, axis (0,0,1), area 8.5mm2, adj f15,f16,f35,f36
  f58: cylinder r=0.87mm len=3.1mm, axis (0,0,1), area 8.5mm2, adj f15,f16,f32,f34
  f59: cylinder r=0.87mm len=3.1mm, axis (0,0,1), area 8.5mm2, adj f15,f16,f32,f33
PART E: 60 faces, bbox 60x90x3.1 mm
  f0: plane 7.64x3.1mm, normal (-1,0,0), area 23.7mm2, adj f15,f16,f30,f31
  f1: plane 3.1x1.87mm, normal (0,1,0), area 5.8mm2, adj f15,f16,f19,f31
  f2: plane 3.1x1.87mm, normal (0,-1,0), area 5.8mm2, adj f15,f16,f18,f30
  f3: plane 7.64x3.1mm, normal (-1,0,0), area 23.7mm2, adj f15,f16,f28,f29
  f4: plane 3.1x1.87mm, normal (0,1,0), area 5.8mm2, adj f15,f16,f18,f29
  f5: plane 3.1x1.87mm, normal (0,-1,0), area 5.8mm2, adj f14,f15,f16,f28
  f6: plane 8.82x3.1mm, normal (0,1,0), area 27.3mm2, adj f14,f15,f16,f27
  f7: plane 3.1x1.87mm, normal (-1,0,0), area 5.8mm2, adj f15,f16,f20,f27
  f8: plane 7.64x3.1mm, normal (0,1,0), area 23.7mm2, adj f15,f16,f25,f26
  f9: plane 3.1x1.87mm, normal (1,0,0), area 5.8mm2, adj f15,f16,f20,f26
  f10: plane 3.1x1.87mm, normal (-1,0,0), area 5.8mm2, adj f15,f16,f21,f25
  f11: plane 7.64x3.1mm, normal (0,1,0), area 23.7mm2, adj f15,f16,f23,f24
  f12: plane 3.1x1.87mm, normal (1,0,0), area 5.8mm2, adj f15,f16,f21,f24
  f13: plane 3.1x1.87mm, normal (-1,0,0), area 5.8mm2, adj f15,f16,f22,f23
  f14: plane 6.85x3.1mm, normal (-1,0,0), area 21.2mm2, adj f5,f6,f15,f16
  f15: plane 90x60mm, normal (0,0,-1), area 5079.4mm2, adj f0,f1,f2,f3,f4,f5,f6,f7
  f16: plane 90x60mm, normal (0,0,1), area 5079.4mm2, adj f0,f1,f2,f3,f4,f5,f6,f7
  f17: plane 90x3.1mm, normal (1,0,0), area 279mm2, adj f15,f16,f22,f50
  f18: plane 9.9x3.1mm, normal (-1,0,0), area 30.7mm2, adj f2,f4,f15,f16
  f19: plane 9.9x3.1mm, normal (-1,0,0), area 30.7mm2, adj f1,f15,f16,f33
  f20: plane 9.9x3.1mm, normal (0,1,0), area 30.7mm2, adj f7,f9,f15,f16
  f21: plane 9.9x3.1mm, normal (0,1,0), area 30.7mm2, adj f10,f12,f15,f16
  f22: plane 9.95x3.1mm, normal (0,1,0), area 30.8mm2, adj f13,f15,f16,f17
  f23: cylinder r=0.87mm len=3.1mm, axis (0,0,1), area 8.5mm2, adj f11,f13,f15,f16
  f24: cylinder r=0.87mm len=3.1mm, axis (0,0,1), area 8.5mm2, adj f11,f12,f15,f16
  f25: cylinder r=0.87mm len=3.1mm, axis (0,0,1), area 8.5mm2, adj f8,f10,f15,f16
  f26: cylinder r=0.87mm len=3.1mm, axis (0,0,1), area 8.5mm2, adj f8,f9,f15,f16
  f27: cylinder r=0.87mm len=3.1mm, axis (0,0,1), area 8.5mm2, adj f6,f7,f15,f16
  f28: cylinder r=0.87mm len=3.1mm, axis (0,0,1), area 8.5mm2, adj f3,f5,f15,f16
  f29: cylinder r=0.87mm len=3.1mm, axis (0,0,1), area 8.5mm2, adj f3,f4,f15,f16
  f30: cylinder r=0.87mm len=3.1mm, axis (0,0,1), area 8.5mm2, adj f0,f2,f15,f16
  f31: cylinder r=0.87mm len=3.1mm, axis (0,0,1), area 8.5mm2, adj f0,f1,f15,f16
  f32: plane 7.64x3.1mm, normal (-1,0,0), area 23.7mm2, adj f15,f16,f58,f59
  f33: plane 3.1x1.87mm, normal (0,-1,0), area 5.8mm2, adj f15,f16,f19,f59
  f34: plane 3.1x1.87mm, normal (0,1,0), area 5.8mm2, adj f15,f16,f47,f58
  f35: plane 7.64x3.1mm, normal (-1,0,0), area 23.7mm2, adj f15,f16,f56,f57
  f36: plane 3.1x1.87mm, normal (0,-1,0), area 5.8mm2, adj f15,f16,f47,f57
  f37: plane 3.1x1.87mm, normal (0,1,0), area 5.8mm2, adj f15,f16,f46,f56
  f38: plane 8.82x3.1mm, normal (0,-1,0), area 27.3mm2, adj f15,f16,f46,f55
  f39: plane 3.1x1.87mm, normal (-1,0,0), area 5.8mm2, adj f15,f16,f48,f55
  f40: plane 7.64x3.1mm, normal (0,-1,0), area 23.7mm2, adj f15,f16,f53,f54
  f41: plane 3.1x1.87mm, normal (1,0,0), area 5.8mm2, adj f15,f16,f48,f54
  f42: plane 3.1x1.87mm, normal (-1,0,0), area 5.8mm2, adj f15,f16,f49,f53
  f43: plane 7.64x3.1mm, normal (0,-1,0), area 23.7mm2, adj f15,f16,f51,f52
  f44: plane 3.1x1.87mm, normal (1,0,0), area 5.8mm2, adj f15,f16,f49,f52
  f45: plane 3.1x1.87mm, normal (-1,0,0), area 5.8mm2, adj f15,f16,f50,f51
  f46: plane 6.85x3.1mm, normal (-1,0,0), area 21.2mm2, adj f15,f16,f37,f38
  f47: plane 9.9x3.1mm, normal (-1,0,0), area 30.7mm2, adj f15,f16,f34,f36
  f48: plane 9.9x3.1mm, normal (0,-1,0), area 30.7mm2, adj f15,f16,f39,f41
  f49: plane 9.9x3.1mm, normal (0,-1,0), area 30.7mm2, adj f15,f16,f42,f44
  f50: plane 9.95x3.1mm, normal (0,-1,0), area 30.8mm2, adj f15,f16,f17,f45
  f51: cylinder r=0.87mm len=3.1mm, axis (0,0,1), area 8.5mm2, adj f15,f16,f43,f45
  f52: cylinder r=0.87mm len=3.1mm, axis (0,0,1), area 8.5mm2, adj f15,f16,f43,f44
  f53: cylinder r=0.87mm len=3.1mm, axis (0,0,1), area 8.5mm2, adj f15,f16,f40,f42
  f54: cylinder r=0.87mm len=3.1mm, axis (0,0,1), area 8.5mm2, adj f15,f16,f40,f41
  f55: cylinder r=0.87mm len=3.1mm, axis (0,0,1), area 8.5mm2, adj f15,f16,f38,f39
  f56: cylinder r=0.87mm len=3.1mm, axis (0,0,1), area 8.5mm2, adj f15,f16,f35,f37
  f57: cylinder r=0.87mm len=3.1mm, axis (0,0,1), area 8.5mm2, adj f15,f16,f35,f36
  f58: cylinder r=0.87mm len=3.1mm, axis (0,0,1), area 8.5mm2, adj f15,f16,f32,f34
  f59: cylinder r=0.87mm len=3.1mm, axis (0,0,1), area 8.5mm2, adj f15,f16,f32,f33
PLACE A t=(-0.26,216.12,0)mm
PLACE B t=(0.26,2.93,0)mm
PLACE C at identity fixed
PLACE D t=(116.64,-93.32,0)mm
PLACE E t=(-117.02,-93.27,0)mm
MATE planar D.f16 <-> C.f15  axis (0,0,1) through (30.74,-93.32,3.1)mm
MATE planar C.f15 <-> E.f16  axis (0,0,1) through (0,0,3.1)mm
MATE planar C.f15 <-> B.f17  axis (0,0,1) through (0,0,3.1)mm
MATE planar C.f15 <-> A.f17  axis (0,0,1) through (0,0,3.1)mm
